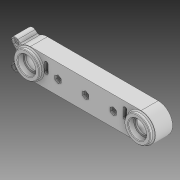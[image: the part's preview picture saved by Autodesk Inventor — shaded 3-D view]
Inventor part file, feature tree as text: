
AUTODESK INVENTOR PART (.ipt)
format: ipt  version: 2020 (Build 240168000, 168)  size: 453,632 bytes
history: native  units: mm
features: extrude x12, sketch x11, projected_geometry x4, chamfer x2, pattern_linear x1, fillet x1
ambient origin geometry x8: Origin, YZ Plane, XZ Plane, XY Plane, X Axis, Y Axis, Z Axis, Center Point
bodies: Solid1 (feature_tree)
feature tree (31):
  extrude  "Extrusion1"  Depth=13.0mm
  extrude  "Extrusion2"  Depth=12.5mm TaperAngle=0.0deg
  extrude  "Extrusion5"  TaperAngle=0.0deg  [1 undecoded]
  extrude  "Extrusion6"  Depth=3.0mm
  extrude  "Extrusion7"  Depth=3.5mm TaperAngle=0.0deg
  chamfer  "Chamfer1"  Distance=5.0mm
  extrude  "Extrusion8"  Depth=1.5mm
  extrude  "Extrusion9"  Depth=3.5mm
  extrude  "Extrusion10"  Depth=0.2mm TaperAngle=0.0deg
  pattern_linear  "Rectangular Pattern1"  Spacing1=1.0mm  [1 undecoded]
  extrude  "Extrusion11"  Depth=1.0mm
  extrude  "Extrusion13"  Depth=25.0mm
  chamfer  "Chamfer2"  Distance=20.0mm
  extrude  "Extrusion15"  Depth=14.5mm
  extrude  "Extrusion14"  Depth=10.0mm TaperAngle=0.0deg
  fillet  "Fillet1"  Radius=4.0mm
  sketch  "Sketch1"  dims[d0=100.3mm d1=13.0mm]
  sketch  "Sketch2"  dims[d2=3.0mm d3=0.0mm d5=12.5mm d6=0.0mm]
  projected_geometry  "Projected Loop1"
  sketch  "Sketch5"  dims[d14=6.0mm d15=0.0mm d16=0.0mm]
  sketch  "Sketch6"  dims[d17=3.0mm d18=16.25mm]
  sketch  "Sketch7"  dims[d19=3.5mm d20=3.5mm d21=0.0mm d22=5.0mm d23=0.0mm]
  sketch  "Sketch8"  dims[d24=1.0mm d25=2.0mm d26=45.0deg d27=1.5mm]
  sketch  "Sketch9"  dims[d28=0.4mm d29=0.0mm d30=3.5mm]
  sketch  "Sketch10"  dims[d31=8.0mm d34=0.2mm d35=0.0mm]
  sketch  "Sketch14"  dims[d36=3.0mm d37=0.0mm]
  projected_geometry  "Projected Loop2"
  projected_geometry  "Projected Loop3"
  projected_geometry  "Projected Loop4"
  sketch  "Sketch15"  dims[d38=1.0mm]
  sketch  "Sketch16"  dims[d39=1.0mm d40=1.0mm d41=1.0mm d42=25.0mm d43=20.0mm d45=100.3mm d47=14.5mm d48=10.0mm d49=0.0mm d50=4.0mm d51=4.0mm d52=4.0mm d53=4.0mm d57=11.5mm d58=0.0mm d59=5.8mm d60=2.0mm d61=0.0mm d62=0.5mm d63=2.0mm d64=45.0deg d65=1.7mm d66=7.0mm d67=25.0mm d68=7.5mm d69=3.2mm d70=10.0mm d71=10.0mm d72=0.0mm d73=2.0mm]
note: 2 required parameter values undecoded (feature->parameter linkage not recoverable at this tier; creation-order binding heuristic only, values carry confidence <= 0.55)
